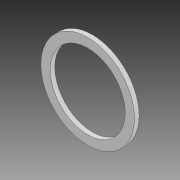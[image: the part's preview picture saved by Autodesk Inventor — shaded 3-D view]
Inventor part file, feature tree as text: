
AUTODESK INVENTOR PART (.ipt)
format: ipt  version: 2020 (Build 240168000, 168)  size: 83,456 bytes
history: native  units: mm
features: extrude x1, sketch x1
ambient origin geometry x8: Origin, YZ Plane, XZ Plane, XY Plane, X Axis, Y Axis, Z Axis, Center Point
bodies: Solid1 (feature_tree)
feature tree (2):
  extrude  "Extrusion1"  Depth=0.5mm
  sketch  "Sketch1"  dims[d0=8.1mm d1=1.0mm d2=0.5mm d3=0.0mm]
